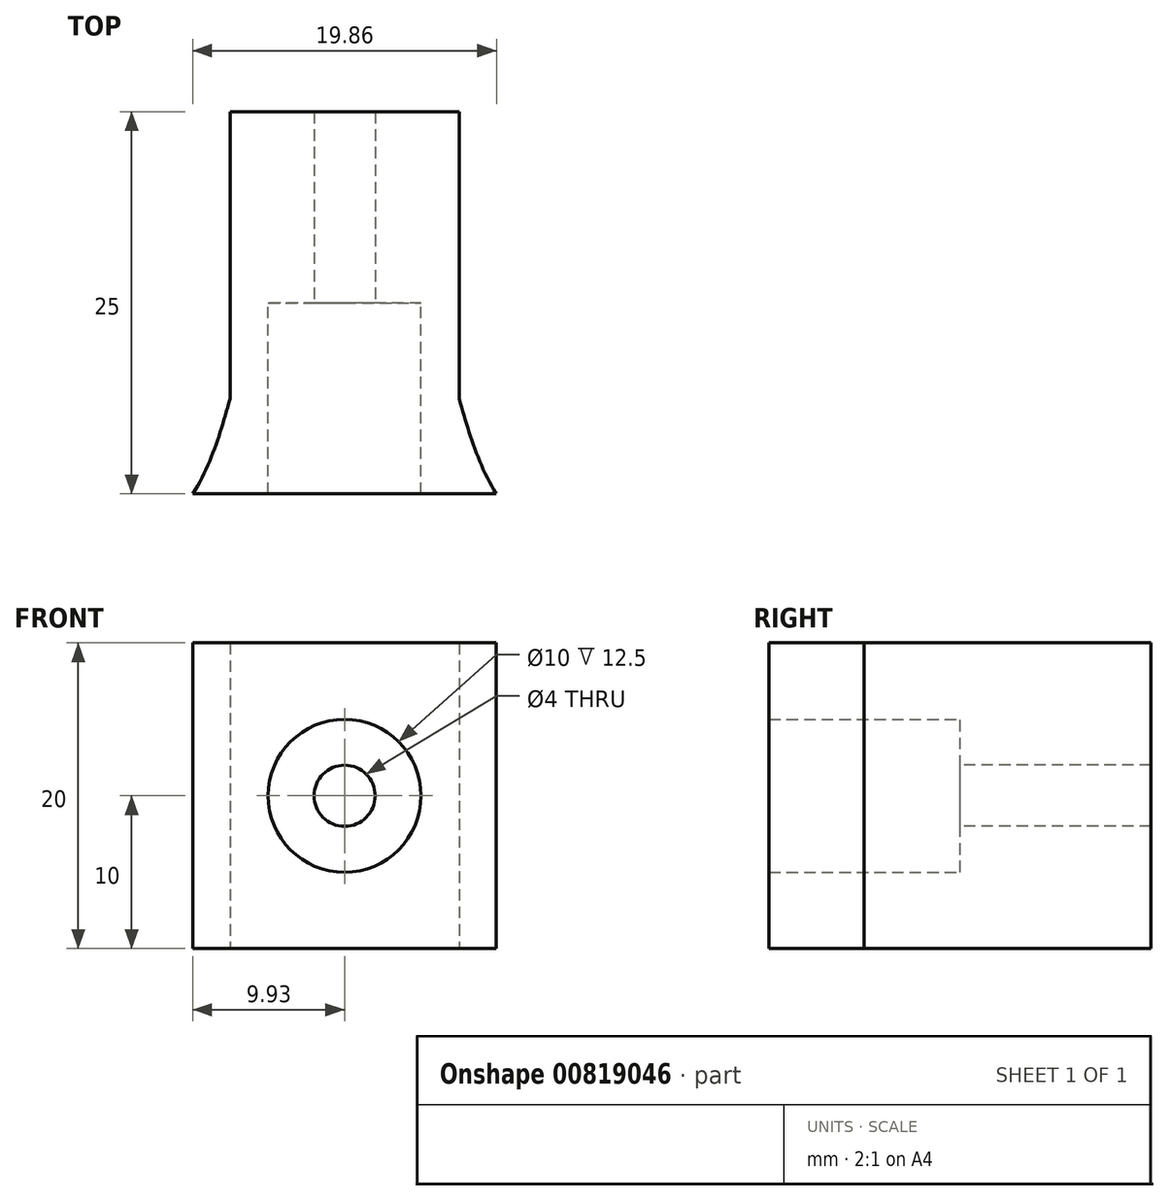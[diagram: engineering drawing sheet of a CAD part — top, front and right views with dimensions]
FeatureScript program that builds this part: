
annotation { "Feature Type Name" : "Feature", "Feature Type Description" : "" }
export const myFeature = defineFeature(function(context is Context, id is Id, definition is map)
    precondition{}
    {
        {
            var Q0;
            Q0=qCreatedBy(makeId("Top.planeOp"),FACE);
            var sketch = newSketch(context, id + "F0", { "sketchPlane" : qUnion([Q0])});
            skLineSegment(sketch, "E0.bottom", {"start": v(-7.5, -12.5) * mm, "end": v(7.5, -12.5) * mm});
            skLineSegment(sketch, "E0.top", {"start": v(-7.5, 12.5) * mm, "end": v(7.5, 12.5) * mm});
            skLineSegment(sketch, "E0.left", {"start": v(-7.5, -6.27) * mm, "end": v(-7.5, 12.5) * mm});
            skLineSegment(sketch, "E0.right", {"start": v(7.5, -6.27) * mm, "end": v(7.5, 12.5) * mm});
            skPoint(sketch, "E0.middle", {"position": v(0, 0) * mm});
            skLineSegment(sketch, "E1", {"start": v(-7.5, -12.5) * mm, "end": v(-9.93, -12.5) * mm});
            skFitSpline(sketch, "E2", {"points": [v(-7.5, -6.27) * mm, v(-9.93, -12.5) * mm, v(-16.3, -19.57) * mm], "startDerivative": vector(-3.87, -13.8) * mm, "endDerivative": vector(-13.44, -12.82) * mm});
            skLineSegment(sketch, "E3", {"start": v(0, 0) * mm, "end": v(0, -4.12) * mm, "construction": true});
            skFitSpline(sketch, "E4.MirrorCS", {"points": [v(7.5, -6.27) * mm, v(9.93, -12.5) * mm, v(16.3, -19.57) * mm], "startDerivative": vector(3.87, -13.8) * mm, "endDerivative": vector(13.44, -12.82) * mm});
            skLineSegment(sketch, "E5.MirrorCS", {"start": v(7.5, -12.5) * mm, "end": v(9.93, -12.5) * mm});
            skSolve(sketch);
        }
        {
            var Q0;
            Q0=makeQuery(id+"F0.imprint","IMPRINT",FACE,{"disambiguationData":[TD([[makeQuery(id+"F0.imprint","IMPRINT",EDGE,{"derivedFrom":sQuery(id+"F0.wireOp",EDGE,"E0.bottom")}),1.0]])]});
            extrude(context, id + "F1", {"entities" : qUnion([Q0]), "depth" : 20 * mm, "offsetDistance" : 25 * mm});
        }
        {
            var Q0;
            Q0=qCreatedBy(makeId("Front.planeOp"),FACE);
            var sketch = newSketch(context, id + "F2", { "sketchPlane" : qUnion([Q0])});
            skLineSegment(sketch, "E6", {"start": v(0, 0) * mm, "end": v(0, 10) * mm, "construction": true});
            skCircle(sketch, "E7", {"center": v(0, 10) * mm, "radius": 2 * mm});
            skCircle(sketch, "E8", {"center": v(0, 10) * mm, "radius": 5 * mm});
            skSolve(sketch);
        }
        {
            var Q0;
            Q0 = qSketchRegion(id + "F2", true);
            var Q1;
            Q1=makeQuery(id+"F2.imprint","IMPRINT",FACE,{"disambiguationData":[TD([[makeQuery(id+"F2.imprint","IMPRINT",EDGE,{"derivedFrom":sQuery(id+"F2.wireOp",EDGE,"E7")}),1.0]])]});
            extrude(context, id + "F3", {"entities" : qUnion([Q0, Q1]), "operationType" : NewBodyOperationType.REMOVE, "depth" : 25 * mm, "offsetDistance" : 25 * mm});
        }
        {
            var Q0;
            Q0=makeQuery(id+"F2.imprint","IMPRINT",FACE,{"disambiguationData":[TD([[makeQuery(id+"F2.imprint","IMPRINT",EDGE,{"derivedFrom":sQuery(id+"F2.wireOp",EDGE,"E7")}),1.0]])]});
            extrude(context, id + "F4", {"entities" : qUnion([Q0]), "operationType" : NewBodyOperationType.REMOVE, "oppositeDirection" : true, "depth" : 25 * mm, "offsetDistance" : 25 * mm});
        }
    });
